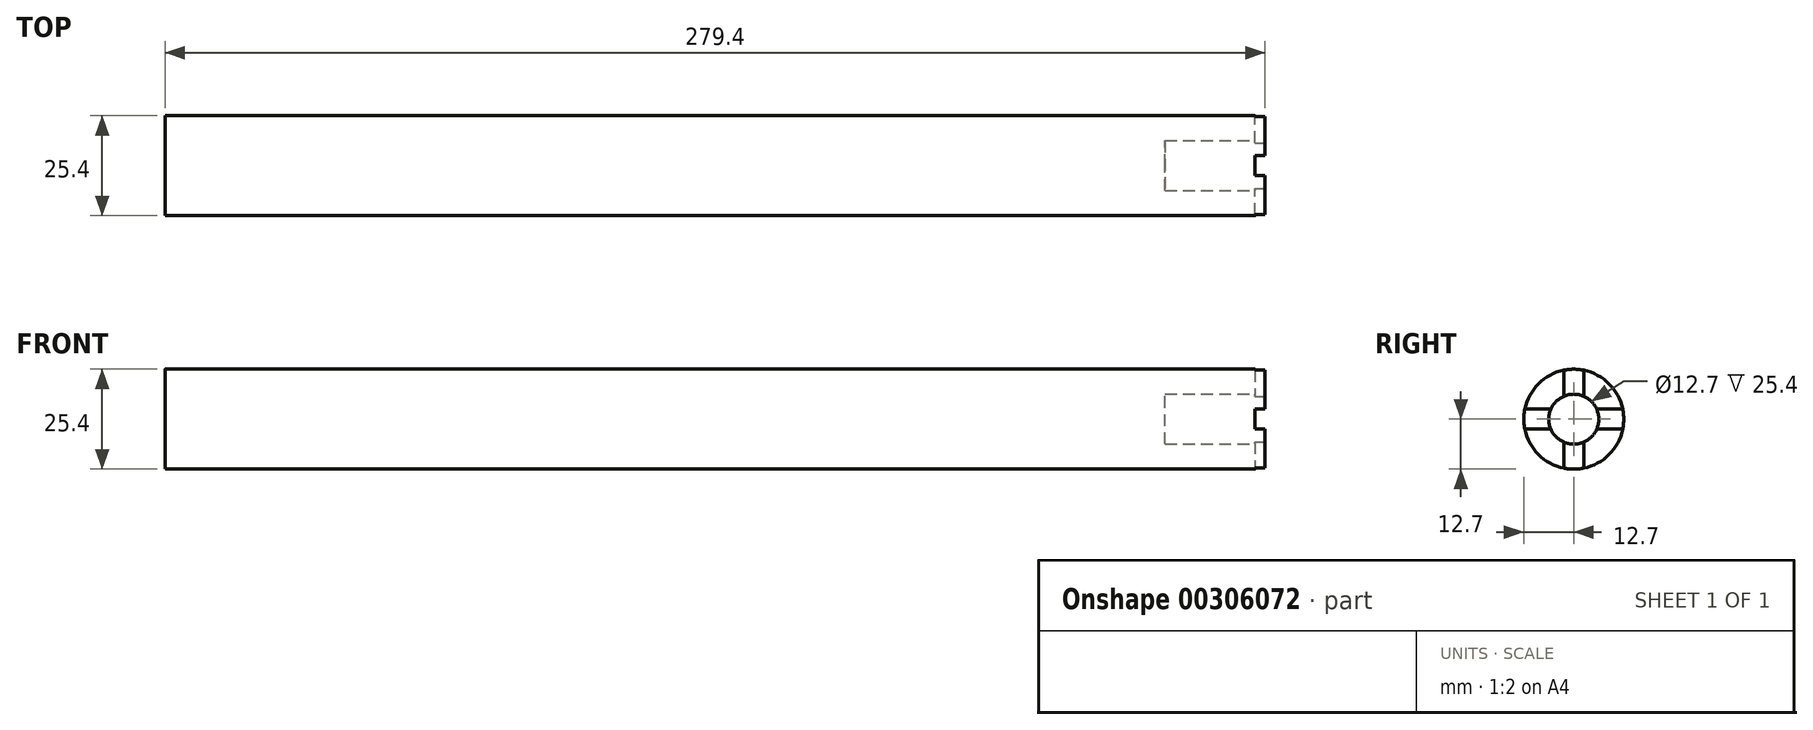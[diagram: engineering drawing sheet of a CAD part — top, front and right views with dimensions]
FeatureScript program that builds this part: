
annotation { "Feature Type Name" : "Feature", "Feature Type Description" : "" }
export const myFeature = defineFeature(function(context is Context, id is Id, definition is map)
    precondition{}
    {
        {
            var Q0;
            Q0=qCreatedBy(makeId("Right.planeOp"),FACE);
            var sketch = newSketch(context, id + "F0", { "sketchPlane" : qUnion([Q0])});
            skCircle(sketch, "E0", {"center": v(0, 0) * mm, "radius": 12.7 * mm});
            skSolve(sketch);
        }
        {
            var Q0;
            Q0 = qSketchRegion(id + "F0", true);
            extrude(context, id + "F1", {"entities" : qUnion([Q0]), "depth" : 279.4 * mm});
        }
        {
            var Q0;
            Q0=makeQuery(id+"F1.opExtrude","CAP_FACE",FACE,{"disambiguationData":[OSD([sQuery(id+"F0.wireOp",EDGE,"E0")])],"isStart":false});
            var sketch = newSketch(context, id + "F2", { "sketchPlane" : qUnion([Q0])});
            skCircle(sketch, "E1", {"center": v(0, 0) * mm, "radius": 6.35 * mm});
            skSolve(sketch);
        }
        {
            var Q0;
            Q0 = qSketchRegion(id + "F2", true);
            extrude(context, id + "F3", {"entities" : qUnion([Q0]), "operationType" : NewBodyOperationType.REMOVE, "oppositeDirection" : true, "depth" : 25.4 * mm});
        }
        {
            var Q0;
            Q0=makeQuery(id+"F1.opExtrude","CAP_FACE",FACE,{"disambiguationData":[OSD([sQuery(id+"F0.wireOp",EDGE,"E0")])],"isStart":false});
            var sketch = newSketch(context, id + "F4", { "sketchPlane" : qUnion([Q0])});
            skLineSegment(sketch, "E2.top", {"start": v(-12.7, 2.54) * mm, "end": v(12.7, 2.54) * mm});
            skLineSegment(sketch, "E2.left", {"start": v(-12.7, 0) * mm, "end": v(-12.7, 2.54) * mm});
            skLineSegment(sketch, "E2.right", {"start": v(12.7, 0) * mm, "end": v(12.7, 2.54) * mm});
            skLineSegment(sketch, "E3.MirrorCS", {"start": v(-12.7, -2.54) * mm, "end": v(12.7, -2.54) * mm});
            skLineSegment(sketch, "E4.MirrorCS", {"start": v(-12.7, 0) * mm, "end": v(-12.7, -2.54) * mm});
            skLineSegment(sketch, "E5.MirrorCS", {"start": v(12.7, 0) * mm, "end": v(12.7, -2.54) * mm});
            skLineSegment(sketch, "E6", {"start": v(0, 12.7) * mm, "end": v(-2.54, 12.7) * mm});
            skLineSegment(sketch, "E7", {"start": v(-2.54, 12.7) * mm, "end": v(-2.54, -12.7) * mm});
            skLineSegment(sketch, "E8", {"start": v(-2.54, -12.7) * mm, "end": v(0, -12.7) * mm});
            skLineSegment(sketch, "E9", {"start": v(0, -12.7) * mm, "end": v(2.54, -12.7) * mm});
            skLineSegment(sketch, "E10", {"start": v(2.54, -12.7) * mm, "end": v(2.54, 12.7) * mm});
            skLineSegment(sketch, "E11", {"start": v(2.54, 12.7) * mm, "end": v(0, 12.7) * mm});
            skSolve(sketch);
        }
        {
            var Q0;
            {var subQ0=makeQuery(id+"F1.opExtrude","CAP_EDGE",EDGE,{"disambiguationData":[OSD([sQuery(id+"F0.wireOp",EDGE,"E0")])],"isStart":false});var subQ4=sQuery(id+"F4.wireOp",EDGE,"E2.top");var subQ5=makeQuery(id+"F4.imprint","INTERSECT",VERTEX,{"disambiguationData":[OD(0.0)],"derivedFrom":[subQ0,subQ4]});Q0=makeQuery(id+"F4.imprint","IMPRINT",FACE,{"disambiguationData":[TD([[makeQuery(id+"F4.imprint","IMPRINT",EDGE,{"disambiguationData":[TD([[subQ5,-1.0]])],"derivedFrom":subQ4}),-1.0]])]});}
            var Q1;
            {var subQ0=makeQuery(id+"F1.opExtrude","CAP_EDGE",EDGE,{"disambiguationData":[OSD([sQuery(id+"F0.wireOp",EDGE,"E0")])],"isStart":false});var subQ4=sQuery(id+"F4.wireOp",EDGE,"E2.top");var subQ5=makeQuery(id+"F4.imprint","INTERSECT",VERTEX,{"disambiguationData":[OD(1.0)],"derivedFrom":[subQ0,subQ4]});Q1=makeQuery(id+"F4.imprint","IMPRINT",FACE,{"disambiguationData":[TD([[makeQuery(id+"F4.imprint","IMPRINT",EDGE,{"disambiguationData":[TD([[subQ5,1.0]])],"derivedFrom":subQ4}),-1.0]])]});}
            var Q2;
            {var subQ0=makeQuery(id+"F1.opExtrude","CAP_EDGE",EDGE,{"disambiguationData":[OSD([sQuery(id+"F0.wireOp",EDGE,"E0")])],"isStart":false});var subQ6=sQuery(id+"F4.wireOp",EDGE,"E7");var subQ7=makeQuery(id+"F4.imprint","INTERSECT",VERTEX,{"disambiguationData":[OD(0.0)],"derivedFrom":[subQ0,subQ6]});Q2=makeQuery(id+"F4.imprint","IMPRINT",FACE,{"disambiguationData":[TD([[makeQuery(id+"F4.imprint","IMPRINT",EDGE,{"disambiguationData":[TD([[subQ7,-1.0]])],"derivedFrom":subQ6}),1.0]])]});}
            var Q3;
            {var subQ0=makeQuery(id+"F1.opExtrude","CAP_EDGE",EDGE,{"disambiguationData":[OSD([sQuery(id+"F0.wireOp",EDGE,"E0")])],"isStart":false});var subQ4=sQuery(id+"F4.wireOp",EDGE,"E7");var subQ5=makeQuery(id+"F4.imprint","INTERSECT",VERTEX,{"disambiguationData":[OD(1.0)],"derivedFrom":[subQ0,subQ4]});Q3=makeQuery(id+"F4.imprint","IMPRINT",FACE,{"disambiguationData":[TD([[makeQuery(id+"F4.imprint","IMPRINT",EDGE,{"disambiguationData":[TD([[subQ5,1.0]])],"derivedFrom":subQ4}),1.0]])]});}
            extrude(context, id + "F5", {"entities" : qUnion([Q0, Q1, Q2, Q3]), "operationType" : NewBodyOperationType.REMOVE, "oppositeDirection" : true, "depth" : 2.54 * mm});
        }
    });
